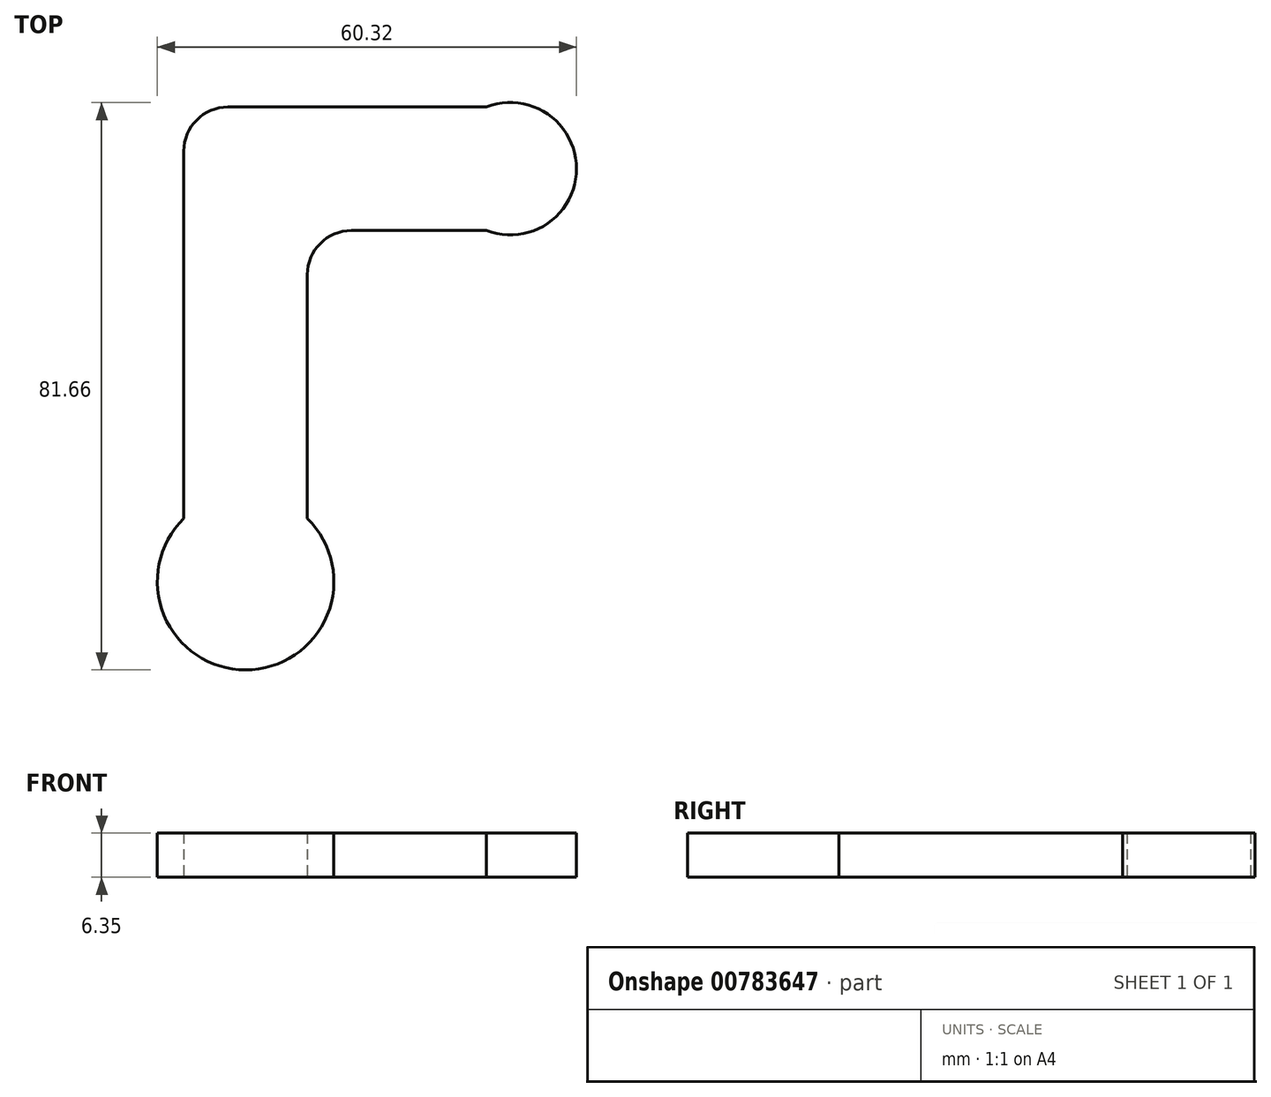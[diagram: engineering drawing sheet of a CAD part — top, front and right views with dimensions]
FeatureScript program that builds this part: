
annotation { "Feature Type Name" : "Feature", "Feature Type Description" : "" }
export const myFeature = defineFeature(function(context is Context, id is Id, definition is map)
    precondition{}
    {
        {
            var Q0;
            Q0=qCreatedBy(makeId("Top.planeOp"),FACE);
            var sketch = newSketch(context, id + "F0", { "sketchPlane" : qUnion([Q0])});
            skArc(sketch, "E0", {"start": v(-8.9, 9.07) * mm, "mid": v(0, -12.7) * mm, "end": v(8.9, 9.07) * mm});
            skPoint(sketch, "E1", {"position": v(12.7, 0) * mm});
            skPoint(sketch, "E2", {"position": v(-12.7, 0) * mm});
            skLineSegment(sketch, "E3", {"start": v(0, 0) * mm, "end": v(0, 59.44) * mm});
            skLineSegment(sketch, "E4.0", {"start": v(8.9, 9.07) * mm, "end": v(8.9, 44.2) * mm});
            skLineSegment(sketch, "E5.0", {"start": v(-8.9, 9.07) * mm, "end": v(-8.9, 61.98) * mm});
            skLineSegment(sketch, "E6", {"start": v(0, 59.44) * mm, "end": v(28.58, 59.44) * mm});
            skLineSegment(sketch, "E7.0", {"start": v(15.24, 50.55) * mm, "end": v(34.68, 50.55) * mm});
            skLineSegment(sketch, "E8.0", {"start": v(-2.54, 68.33) * mm, "end": v(34.68, 68.33) * mm});
            skArc(sketch, "E9", {"start": v(34.68, 50.55) * mm, "mid": v(47.62, 59.44) * mm, "end": v(34.68, 68.33) * mm});
            skArc(sketch, "E10.filletArc", {"start": v(15.24, 50.55) * mm, "mid": v(10.75, 48.69) * mm, "end": v(8.89, 44.2) * mm});
            skArc(sketch, "E11", {"start": v(-2.54, 68.33) * mm, "mid": v(-7.03, 66.47) * mm, "end": v(-8.9, 61.98) * mm});
            skArc(sketch, "E12", {"start": v(-8.9, 9.07) * mm, "mid": v(0, 12.7) * mm, "end": v(8.9, 9.07) * mm});
            skSolve(sketch);
        }
        {
            var Q0;
            Q0 = qSketchRegion(id + "F0", true);
            extrude(context, id + "F1", {"entities" : qUnion([Q0]), "depth" : 6.35 * mm, "offsetDistance" : 25.4 * mm});
        }
    });
